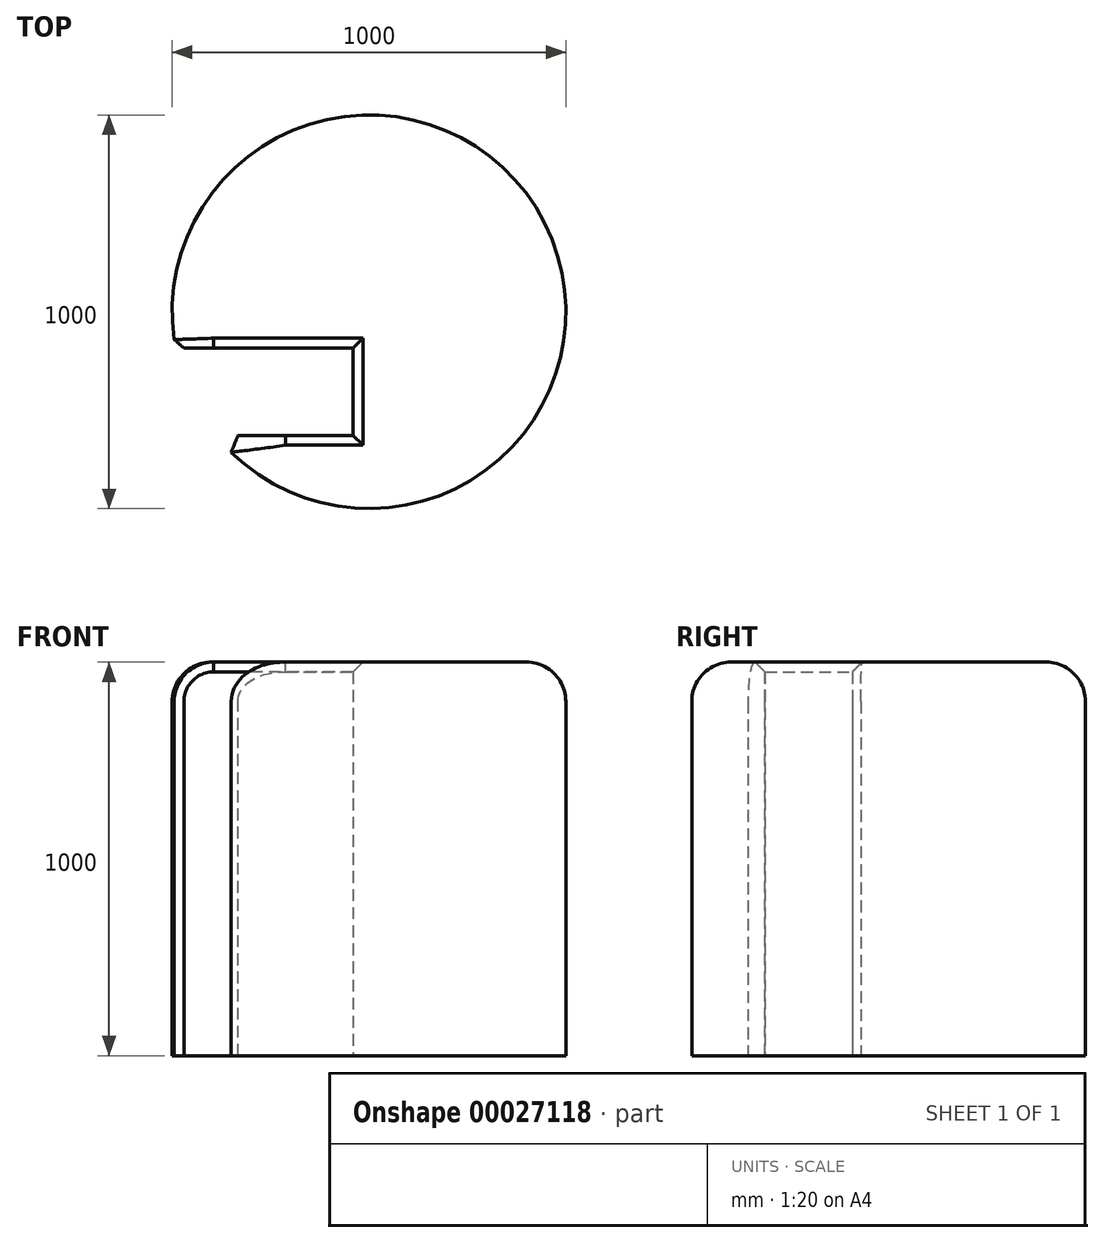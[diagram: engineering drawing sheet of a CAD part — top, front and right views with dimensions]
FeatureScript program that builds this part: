
annotation { "Feature Type Name" : "Feature", "Feature Type Description" : "" }
export const myFeature = defineFeature(function(context is Context, id is Id, definition is map)
    precondition{}
    {
        {
            var Q0;
            Q0=qCreatedBy(makeId("Top.planeOp"),FACE);
            var sketch = newSketch(context, id + "F0", { "sketchPlane" : qUnion([Q0])});
            skCircle(sketch, "E0", {"center": v(54.8, -7.23) * mm, "radius": 500 * mm});
            skLineSegment(sketch, "E1.bottom", {"start": v(-574.37, -321.37) * mm, "end": v(14.58, -321.37) * mm});
            skLineSegment(sketch, "E1.top", {"start": v(-574.37, -99.23) * mm, "end": v(14.58, -99.23) * mm});
            skLineSegment(sketch, "E1.left", {"start": v(-574.37, -321.37) * mm, "end": v(-574.37, -99.23) * mm});
            skLineSegment(sketch, "E1.right", {"start": v(14.58, -321.37) * mm, "end": v(14.58, -99.23) * mm});
            skSolve(sketch);
        }
        {
            var Q0;
            {var subQ0=sQuery(id+"F0.wireOp",EDGE,"E1.right");Q0=makeQuery(id+"F0.imprint","IMPRINT",FACE,{"disambiguationData":[TD([[makeQuery(id+"F0.imprint","IMPRINT",EDGE,{"derivedFrom":subQ0}),-1.0]])]});}
            extrude(context, id + "F1", {"entities" : qUnion([Q0]), "depth" : 1000 * mm});
        }
        {
            var Q0;
            Q0=makeQuery(id+"F1.opExtrude","CAP_EDGE",EDGE,{"disambiguationData":[OSD([sQuery(id+"F0.wireOp",EDGE,"E0")])],"isStart":false});
            fillet(context, id + "F2", {"entities" : qUnion([Q0]), "radius" : 100 * mm, "tangentPropagation" : true, "allowEdgeOverflow" : false});
        }
        {
            var Q0;
            Q0=makeQuery(id+"F1.opExtrude","SWEPT_EDGE",EDGE,{"disambiguationData":[OSD([sQuery(id+"F0.wireOp",EDGE,"E0"),sQuery(id+"F0.wireOp",EDGE,"E1.top")])]});
            var Q1;
            Q1=makeQuery(id+"F1.opExtrude","CAP_EDGE",EDGE,{"disambiguationData":[OSD([sQuery(id+"F0.wireOp",EDGE,"E1.right")])],"isStart":false});
            var Q2;
            Q2=makeQuery(id+"F1.opExtrude","SWEPT_EDGE",EDGE,{"disambiguationData":[OSD([sQuery(id+"F0.wireOp",EDGE,"E0"),sQuery(id+"F0.wireOp",EDGE,"E1.bottom")])]});
            chamfer(context, id + "F3", {"entities" : qUnion([Q0, Q1, Q2]), "width" : 25 * mm, "tangentPropagation" : true});
        }
    });
